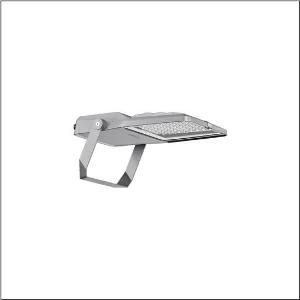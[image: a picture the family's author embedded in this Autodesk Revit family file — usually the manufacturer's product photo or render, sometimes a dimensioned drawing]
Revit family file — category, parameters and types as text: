
# Revit family: floodlight_fl_21_mini___pl33t_5xa7775d2f1a_0460
name_source: partatom
category: Lighting Fixtures
units: mm (PartAtom-declared; Revit-internal decimal feet)

## family parameters
Cut with Voids When Loaded = No
Host = Face
Light Source = No
Part Type = Normal
Room Calculation Point = No
Round Connector Dimension = Use Diameter
Shared = No

## types (1)
- --- (1 x LED, 17630 lm, 142.9 W, 3000K)
    Apparent Load = 143 VA
    CIE Flux Codes = 26 75 99 100 100
    Color Rendering = 70
    Color Temperature = 3000K
    Default Elevation = 1800 mm
    Description = Floodlight FL 21 mini, floodlight, primary light control with lens, of PMMA, primary optical cover: protective disc, of toughened safety glass, transparent, light distribution: PL33T, light emission: direct distribution, installation type: surface-mounted, LED, High Power LED, rated luminous flux: 17.630lm, luminous efficacy: 123lm/W, light colour: 730, colour temperature: 3000K, control: flexible luminous flux parameterisation, time-dependent luminous flux control, constant luminous flux control, overheat protection, presetting dimming logarithmic, with terminal, 6-pole, mains connection: 220..240V, AC, 50/60Hz, start of lifetime: 143W, end of service life: 151W, reduction: 63W, luminaire housing, of diecast aluminium, powder-coated, Siteco® metallic grey (DB 702S), corrosivity category C5 mid according to DIN EN ISO 12944, sealing non-destructively replaceable, mounting bracket, of steel, galvanised, powder-coated, Siteco® metallic grey (DB 702S), Smart Interface above, protection rating (complete): IP66, insulation class (complete): insulation class II (safety insulation), certification: CE, ENEC, VDE, protection symbol: D, impact resistance: IK08, permissible operating ambient temperature: -40..+40°C, permissible operating ambient temperature for outdoor applications: -40..+50°C, standard: DIN EN 12944, LABS conformity tested according to VDMA 24364:2018-05, packaging unit: 1 piece

Light Distribution: PL33T
    Height = 70 mm
    Lamp = 1 x LED
    Lamp Light Flux = 17630 lm
    Lamp Power = 142.9 W
    Lamp count = 1
    Length = 485 mm
    Luminous efficacy = 123 lm/W
    Manufacturer = Siteco
    ModVariant = No
    Model = 5XA7775D2F1A
    Number of Poles = 1
    OnlyDefault = Yes
    Power Factor = 1
    Product Name = Floodlight FL 21 mini | PL33T
    Product group = floodlight | pylon annexe
    ProductGroupID = 6200
    Protection Class = Protection class II
    Protection Degree = IP 66
    RLX_Detail_Level = 1
    RLX_Emergency_Light_Flux = 0 lm
    RLX_Emergency_Type = 0
    RLX_Emergency_Type_DB = No
    RlxData = <blob elided: 96237 chars, md5=296f71db>
    Socket = socket
    Standby Power = 0 W
    System Light Flux = 17630 lm
    System Power = 143 W
    Type Comments = factory setting: luminous flux: 100 % | dim-lin: 254 | 730 mA
    Type Image = l_1006845.jpg
    URL = http://relux.com
    VarID = @adj_080925
    Voltage = 0 V
    Weight = 0.00 kg
    Width = 337 mm

## geometry (parser evidence)
native form markers: Blend x4, Sweep x14
no freeform markers — native parametric forms only
